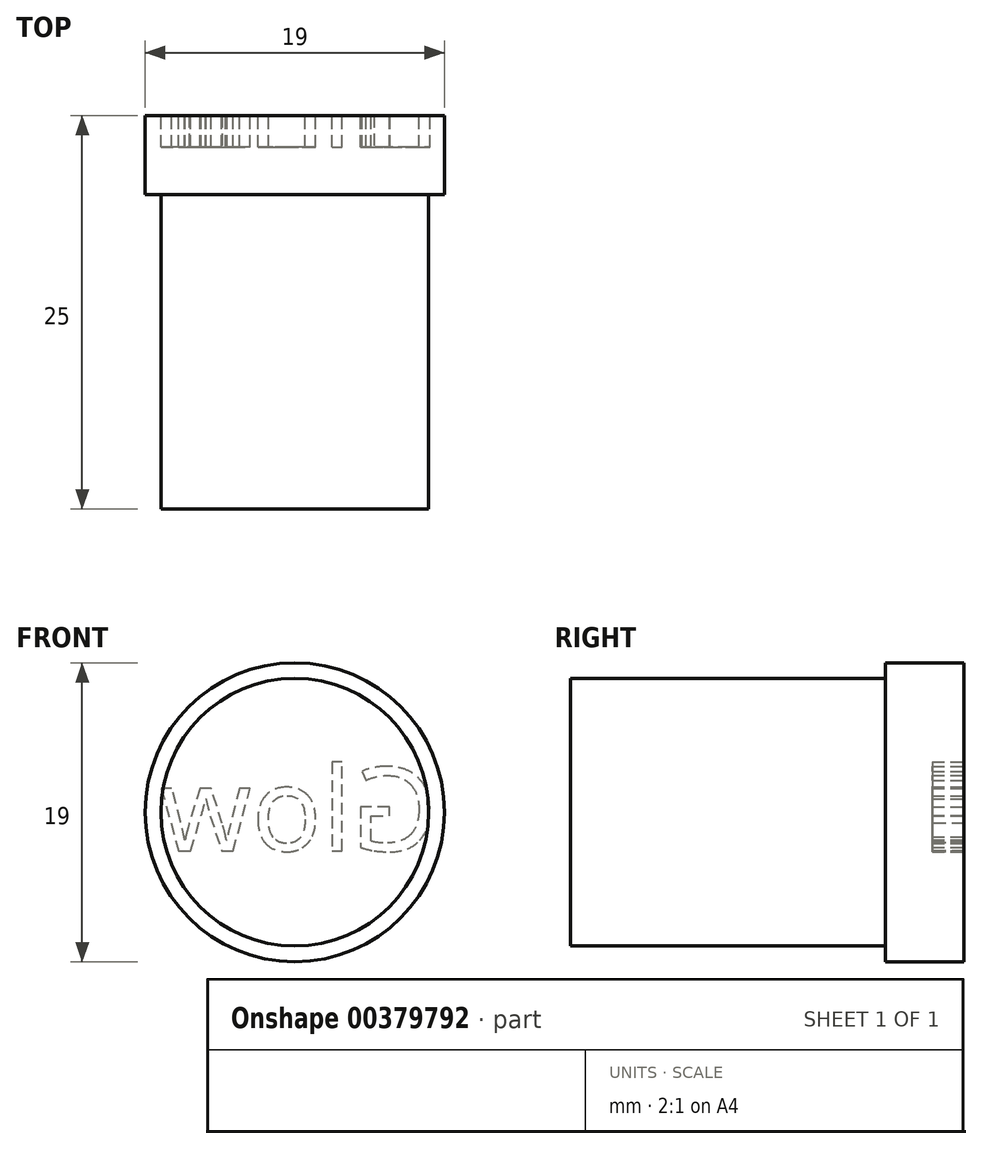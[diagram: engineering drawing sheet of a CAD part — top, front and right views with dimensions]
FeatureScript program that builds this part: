
annotation { "Feature Type Name" : "Feature", "Feature Type Description" : "" }
export const myFeature = defineFeature(function(context is Context, id is Id, definition is map)
    precondition{}
    {
        {
            var Q0;
            Q0=qCreatedBy(makeId("Front.planeOp"),FACE);
            var sketch = newSketch(context, id + "F0", { "sketchPlane" : qUnion([Q0])});
            skCircle(sketch, "E0", {"center": v(0, 0) * mm, "radius": 8.5 * mm});
            skSolve(sketch);
        }
        {
            var Q0;
            Q0=makeQuery(id+"F0.imprint","IMPRINT",FACE,{"disambiguationData":[TD([[makeQuery(id+"F0.imprint","IMPRINT",EDGE,{"derivedFrom":sQuery(id+"F0.wireOp",EDGE,"E0")}),1.0]])]});
            extrude(context, id + "F1", {"entities" : qUnion([Q0]), "depth" : 20 * mm, "offsetDistance" : 25 * mm});
        }
        {
            var Q0;
            Q0=qCreatedBy(makeId("Front.planeOp"),FACE);
            var sketch = newSketch(context, id + "F2", { "sketchPlane" : qUnion([Q0])});
            skCircle(sketch, "E1", {"center": v(0, 0) * mm, "radius": 9.5 * mm});
            skSolve(sketch);
        }
        {
            var Q0;
            Q0=makeQuery(id+"F2.imprint","IMPRINT",FACE,{"disambiguationData":[TD([[makeQuery(id+"F2.imprint","IMPRINT",EDGE,{"derivedFrom":sQuery(id+"F2.wireOp",EDGE,"E1")}),1.0]])]});
            extrude(context, id + "F3", {"entities" : qUnion([Q0]), "operationType" : NewBodyOperationType.ADD, "oppositeDirection" : true, "depth" : 5 * mm, "offsetDistance" : 25 * mm});
        }
        {
            var Q0;
            Q0=makeQuery(id+"F3.opExtrude","CAP_FACE",FACE,{"disambiguationData":[OSD([sQuery(id+"F2.wireOp",EDGE,"E1")])],"isStart":false});
            var sketch = newSketch(context, id + "F4", { "sketchPlane" : qUnion([Q0])});
            skText(sketch, "E2", { "text": "Glow", "fontName": "NotoSans-Regular.ttf"});
            const initialGuessF4  = {"E2": [-0.00903, -0.00244, 1, 0, 0.00533]};
            skSetInitialGuess(sketch, initialGuessF4);
            skSolve(sketch);
        }
        {
            var Q0;
            Q0 = qSketchRegion(id + "F4", true);
            extrude(context, id + "F5", {"entities" : qUnion([Q0]), "operationType" : NewBodyOperationType.REMOVE, "oppositeDirection" : true, "depth" : 2 * mm, "offsetDistance" : 25 * mm});
        }
    });
